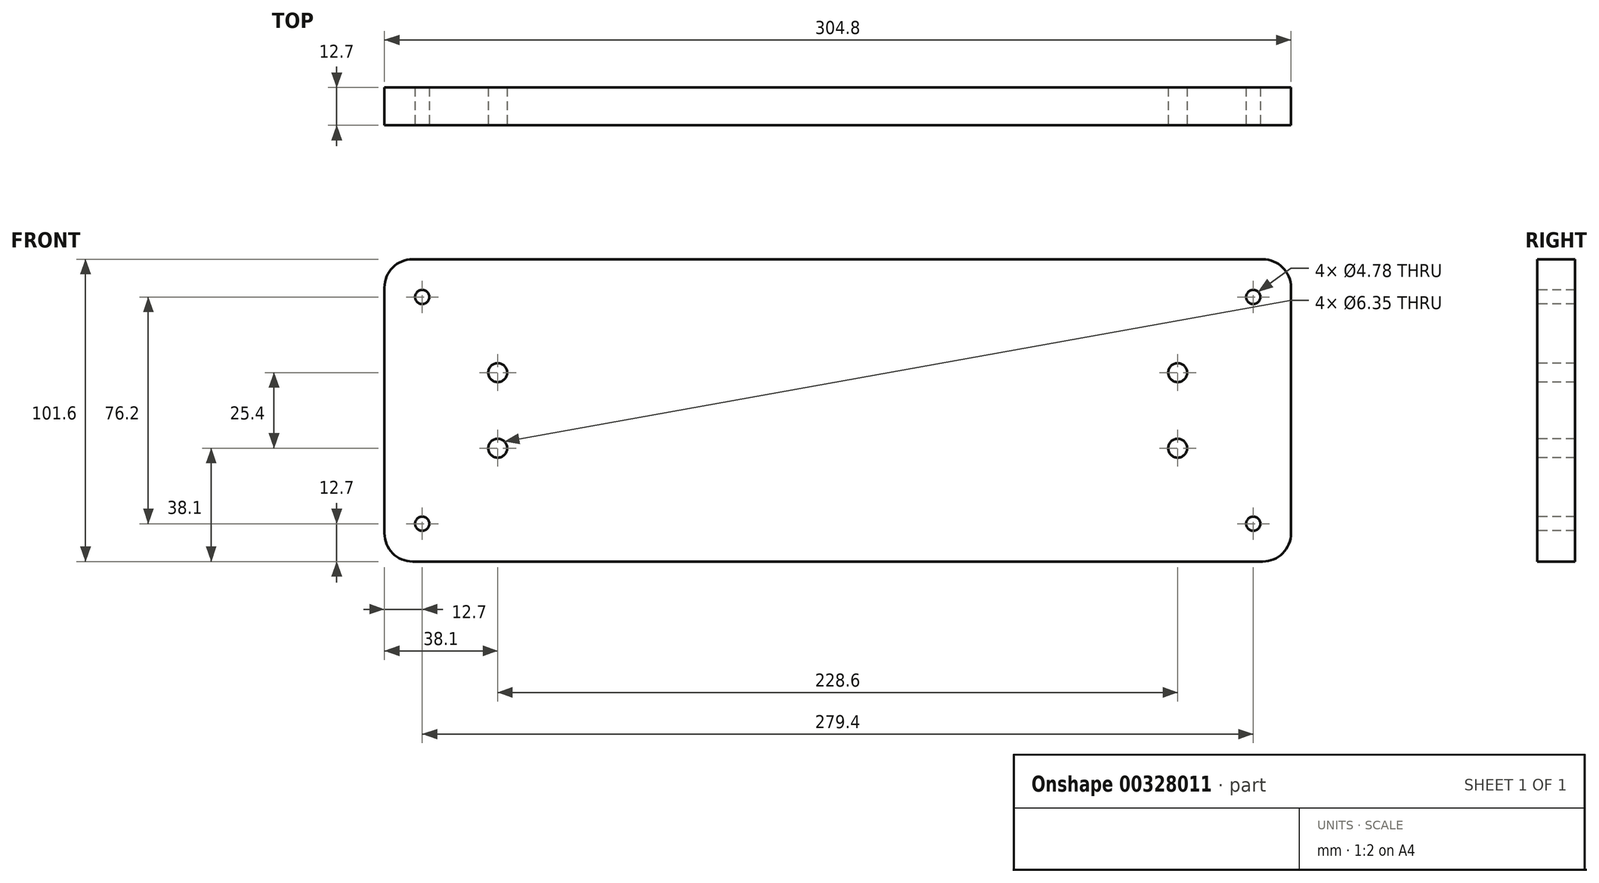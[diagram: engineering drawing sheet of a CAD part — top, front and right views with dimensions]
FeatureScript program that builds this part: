
annotation { "Feature Type Name" : "Feature", "Feature Type Description" : "" }
export const myFeature = defineFeature(function(context is Context, id is Id, definition is map)
    precondition{}
    {
        {
            var Q0;
            Q0=qCreatedBy(makeId("Front.planeOp"),FACE);
            var sketch = newSketch(context, id + "F0", { "sketchPlane" : qUnion([Q0])});
            skLineSegment(sketch, "E0.bottom", {"start": v(0, 0) * mm, "end": v(304.8, 0) * mm});
            skLineSegment(sketch, "E0.top", {"start": v(0, 101.6) * mm, "end": v(304.8, 101.6) * mm});
            skLineSegment(sketch, "E0.left", {"start": v(0, 0) * mm, "end": v(0, 101.6) * mm});
            skLineSegment(sketch, "E0.right", {"start": v(304.8, 0) * mm, "end": v(304.8, 101.6) * mm});
            skSolve(sketch);
        }
        {
            var Q0;
            Q0 = qSketchRegion(id + "F0", true);
            extrude(context, id + "F1", {"entities" : qUnion([Q0]), "depth" : 12.7 * mm});
        }
        {
            var Q0;
            Q0=makeQuery(id+"F1.opExtrude","SWEPT_EDGE",EDGE,{"disambiguationData":[OSD([sQuery(id+"F0.wireOp",EDGE,"E0.top"),sQuery(id+"F0.wireOp",EDGE,"E0.left")])]});
            var Q1;
            Q1=makeQuery(id+"F1.opExtrude","SWEPT_EDGE",EDGE,{"disambiguationData":[OSD([sQuery(id+"F0.wireOp",EDGE,"E0.bottom"),sQuery(id+"F0.wireOp",EDGE,"E0.left")])]});
            var Q2;
            Q2=makeQuery(id+"F1.opExtrude","SWEPT_EDGE",EDGE,{"disambiguationData":[OSD([sQuery(id+"F0.wireOp",EDGE,"E0.bottom"),sQuery(id+"F0.wireOp",EDGE,"E0.right")])]});
            var Q3;
            Q3=makeQuery(id+"F1.opExtrude","SWEPT_EDGE",EDGE,{"disambiguationData":[OSD([sQuery(id+"F0.wireOp",EDGE,"E0.top"),sQuery(id+"F0.wireOp",EDGE,"E0.right")])]});
            fillet(context, id + "F2", {"entities" : qUnion([Q0, Q1, Q2, Q3]), "radius" : 9.52 * mm, "tangentPropagation" : true, "allowEdgeOverflow" : false});
        }
        {
            var Q0;
            Q0=makeQuery(id+"F1.opExtrude","CAP_FACE",FACE,{"disambiguationData":[OSD([sQuery(id+"F0.wireOp",EDGE,"E0.bottom"),sQuery(id+"F0.wireOp",EDGE,"E0.top"),sQuery(id+"F0.wireOp",EDGE,"E0.left"),sQuery(id+"F0.wireOp",EDGE,"E0.right")])],"isStart":false});
            var sketch = newSketch(context, id + "F3", { "sketchPlane" : qUnion([Q0])});
            skPoint(sketch, "E1", {"position": v(12.7, 88.9) * mm});
            skPoint(sketch, "E2", {"position": v(12.7, 12.7) * mm});
            skPoint(sketch, "E3", {"position": v(292.1, 88.9) * mm});
            skPoint(sketch, "E4", {"position": v(292.1, 12.7) * mm});
            skSolve(sketch);
        }
        {
            var Q0;
            Q0=sQuery(id+"F3.wireOp",VERTEX,"E1");
            var Q1;
            Q1=sQuery(id+"F3.wireOp",VERTEX,"E2");
            var Q2;
            Q2=sQuery(id+"F3.wireOp",VERTEX,"E4");
            var Q3;
            Q3=sQuery(id+"F3.wireOp",VERTEX,"E3");
            var Q4;
            Q4=makeQuery(id+"F1.opExtrude","SWEPT_BODY",BODY,{"disambiguationData":[OSD([sQuery(id+"F0.wireOp",EDGE,"E0.bottom"),sQuery(id+"F0.wireOp",EDGE,"E0.top"),sQuery(id+"F0.wireOp",EDGE,"E0.left"),sQuery(id+"F0.wireOp",EDGE,"E0.right")])]});
            hole(context, id + "F4", {"style" : HoleStyle.SIMPLE, "endStyle" : HoleEndStyle.THROUGH, "holeDiameter" : 4.78 * mm, "tappedDepth" : 12.7 * mm, "tapClearance" : 3, "locations" : qUnion([Q0, Q1, Q2, Q3]), "scope" : qUnion([Q4])});
        }
        {
            var Q0;
            Q0=makeQuery(id+"F1.opExtrude","CAP_FACE",FACE,{"disambiguationData":[OSD([sQuery(id+"F0.wireOp",EDGE,"E0.bottom"),sQuery(id+"F0.wireOp",EDGE,"E0.top"),sQuery(id+"F0.wireOp",EDGE,"E0.left"),sQuery(id+"F0.wireOp",EDGE,"E0.right")])],"isStart":false});
            var sketch = newSketch(context, id + "F5", { "sketchPlane" : qUnion([Q0])});
            skPoint(sketch, "E5", {"position": v(38.1, 63.5) * mm});
            skPoint(sketch, "E6", {"position": v(38.1, 38.1) * mm});
            skPoint(sketch, "E7", {"position": v(266.7, 38.1) * mm});
            skPoint(sketch, "E8", {"position": v(266.7, 63.5) * mm});
            skSolve(sketch);
        }
        {
            var Q0;
            Q0=sQuery(id+"F5.wireOp",VERTEX,"E5");
            var Q1;
            Q1=sQuery(id+"F5.wireOp",VERTEX,"E6");
            var Q2;
            Q2=sQuery(id+"F5.wireOp",VERTEX,"E8");
            var Q3;
            Q3=sQuery(id+"F5.wireOp",VERTEX,"E7");
            var Q4;
            Q4=makeQuery(id+"F1.opExtrude","SWEPT_BODY",BODY,{"disambiguationData":[OSD([sQuery(id+"F0.wireOp",EDGE,"E0.bottom"),sQuery(id+"F0.wireOp",EDGE,"E0.top"),sQuery(id+"F0.wireOp",EDGE,"E0.left"),sQuery(id+"F0.wireOp",EDGE,"E0.right")])]});
            hole(context, id + "F6", {"style" : HoleStyle.SIMPLE, "endStyle" : HoleEndStyle.THROUGH, "holeDiameter" : 6.35 * mm, "tappedDepth" : 12.7 * mm, "tapClearance" : 3, "locations" : qUnion([Q0, Q1, Q2, Q3]), "scope" : qUnion([Q4])});
        }
    });
